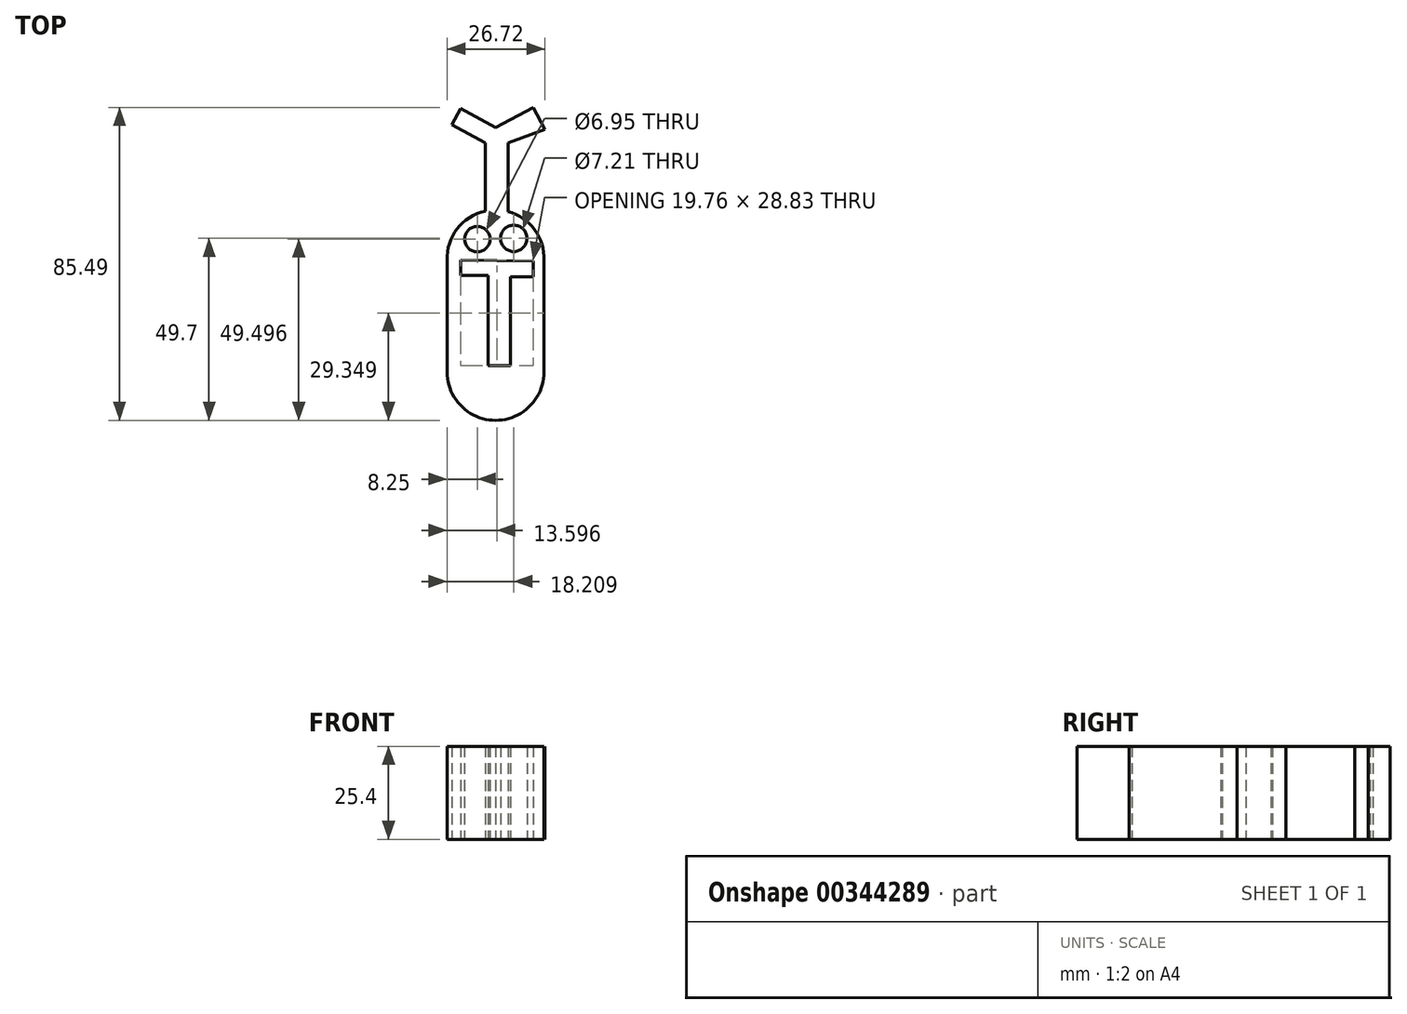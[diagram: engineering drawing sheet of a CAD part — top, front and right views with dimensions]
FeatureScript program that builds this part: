
annotation { "Feature Type Name" : "Feature", "Feature Type Description" : "" }
export const myFeature = defineFeature(function(context is Context, id is Id, definition is map)
    precondition{}
    {
        {
            var Q0;
            Q0=qCreatedBy(makeId("Top.planeOp"),FACE);
            var sketch = newSketch(context, id + "F0", { "sketchPlane" : qUnion([Q0])});
            skPoint(sketch, "E0.center.orphan", {"position": v(0, 27.05) * mm});
            skPoint(sketch, "E1.center.orphan", {"position": v(0, 56.4) * mm});
            skArc(sketch, "E2", {"start": v(13.2, 35.13) * mm, "mid": v(10.66, 43.57) * mm, "end": v(3.38, 48.54) * mm});
            skLineSegment(sketch, "E3", {"start": v(-13.2, 35.14) * mm, "end": v(-13.2, 5.11) * mm});
            skLineSegment(sketch, "E4", {"start": v(13.2, 35.13) * mm, "end": v(13.2, 5.67) * mm});
            skPoint(sketch, "E5.center.orphan", {"position": v(0, 4.74) * mm});
            skArc(sketch, "E6", {"start": v(-13.2, 5.66) * mm, "mid": v(0, -8.5) * mm, "end": v(13.2, 5.67) * mm});
            skLineSegment(sketch, "E7", {"start": v(-9.52, 31.1) * mm, "end": v(-2.08, 31.1) * mm});
            skLineSegment(sketch, "E8", {"start": v(-2.08, 31.1) * mm, "end": v(-2.08, 6.45) * mm});
            skLineSegment(sketch, "E9", {"start": v(-2.08, 6.45) * mm, "end": v(4.08, 6.45) * mm});
            skLineSegment(sketch, "E10", {"start": v(4.08, 6.45) * mm, "end": v(4.08, 30.74) * mm});
            skLineSegment(sketch, "E11", {"start": v(4.08, 30.74) * mm, "end": v(10.25, 30.74) * mm});
            skLineSegment(sketch, "E12", {"start": v(10.25, 30.74) * mm, "end": v(10.25, 35.1) * mm});
            skLineSegment(sketch, "E13", {"start": v(-9.52, 31.1) * mm, "end": v(-9.52, 35.27) * mm});
            skLineSegment(sketch, "E14", {"start": v(-9.52, 35.27) * mm, "end": v(10.25, 35.1) * mm});
            skLineSegment(sketch, "E15", {"start": v(-2.83, 48.67) * mm, "end": v(-2.83, 67.26) * mm});
            skLineSegment(sketch, "E16", {"start": v(-2.83, 67.26) * mm, "end": v(-11.95, 72.25) * mm});
            skLineSegment(sketch, "E17", {"start": v(-11.95, 72.25) * mm, "end": v(-9.52, 76.7) * mm});
            skLineSegment(sketch, "E18", {"start": v(-9.52, 76.7) * mm, "end": v(0, 71.49) * mm});
            skLineSegment(sketch, "E19", {"start": v(0, 71.49) * mm, "end": v(10.25, 77) * mm});
            skLineSegment(sketch, "E20", {"start": v(10.25, 77) * mm, "end": v(13.5, 70.96) * mm});
            skLineSegment(sketch, "E21", {"start": v(13.5, 70.96) * mm, "end": v(3.38, 67.27) * mm});
            skLineSegment(sketch, "E22", {"start": v(3.38, 67.27) * mm, "end": v(3.38, 48.54) * mm});
            skArc(sketch, "E23.trimOffspring", {"start": v(-2.83, 48.67) * mm, "mid": v(-10.5, 43.8) * mm, "end": v(-13.2, 35.14) * mm});
            skCircle(sketch, "E24", {"center": v(-4.98, 41) * mm, "radius": 3.47 * mm});
            skCircle(sketch, "E25", {"center": v(4.98, 41.2) * mm, "radius": 3.6 * mm});
            skSolve(sketch);
        }
        {
            var Q0;
            Q0 = qSketchRegion(id + "F0", true);
            extrude(context, id + "F1", {"entities" : qUnion([Q0]), "depth" : 25.4 * mm});
        }
    });
